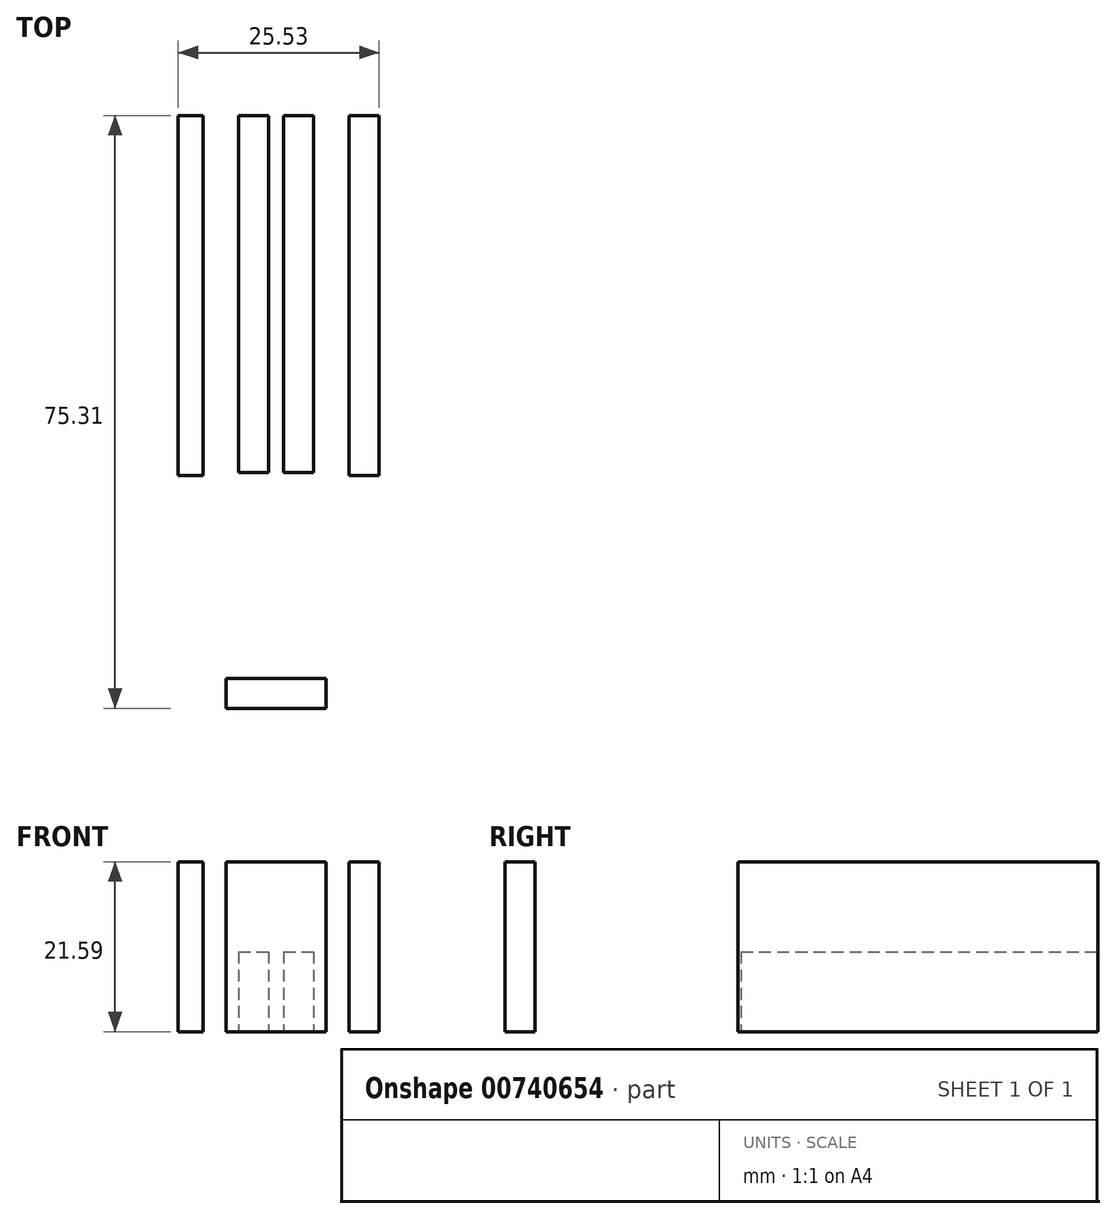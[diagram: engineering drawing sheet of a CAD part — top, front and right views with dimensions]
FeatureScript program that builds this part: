
annotation { "Feature Type Name" : "Feature", "Feature Type Description" : "" }
export const myFeature = defineFeature(function(context is Context, id is Id, definition is map)
    precondition{}
    {
        {
            var Q0;
            Q0=qCreatedBy(makeId("Top.planeOp"),FACE);
            var sketch = newSketch(context, id + "F0", { "sketchPlane" : qUnion([Q0])});
            skLineSegment(sketch, "E0", {"start": v(-8.9, 0) * mm, "end": v(8.9, 0) * mm});
            skLineSegment(sketch, "E1", {"start": v(8.9, 0) * mm, "end": v(7.62, -25.4) * mm});
            skLineSegment(sketch, "E2", {"start": v(7.62, -25.4) * mm, "end": v(-7.62, -25.4) * mm});
            skLineSegment(sketch, "E3", {"start": v(-8.9, 0) * mm, "end": v(-7.62, -25.4) * mm});
            skPoint(sketch, "E4", {"position": v(0, -25.4) * mm});
            skLineSegment(sketch, "E5", {"start": v(-15.24, -25.4) * mm, "end": v(15.24, -25.4) * mm});
            skLineSegment(sketch, "E6", {"start": v(-15.24, -25.4) * mm, "end": v(-15.24, -7.62) * mm});
            skLineSegment(sketch, "E7", {"start": v(-15.24, -7.62) * mm, "end": v(15.24, -7.62) * mm});
            skLineSegment(sketch, "E8", {"start": v(15.24, -7.62) * mm, "end": v(15.24, -25.4) * mm});
            skLineSegment(sketch, "E9", {"start": v(-15.24, -25.4) * mm, "end": v(-19.78, -36.35) * mm});
            skLineSegment(sketch, "E10", {"start": v(-19.78, -36.35) * mm, "end": v(-12.16, -36.35) * mm});
            skLineSegment(sketch, "E11", {"start": v(-12.16, -36.35) * mm, "end": v(-7.62, -25.4) * mm});
            skLineSegment(sketch, "E12.MirrorCS", {"start": v(12.16, -36.35) * mm, "end": v(7.62, -25.4) * mm});
            skLineSegment(sketch, "E13.MirrorCS", {"start": v(19.78, -36.35) * mm, "end": v(12.16, -36.35) * mm});
            skLineSegment(sketch, "E14.MirrorCS", {"start": v(15.24, -25.4) * mm, "end": v(19.78, -36.35) * mm});
            skSolve(sketch);
        }
        {
            var Q0;
            Q0=qCreatedBy(makeId("Top.planeOp"),FACE);
            var sketch = newSketch(context, id + "F1", { "sketchPlane" : qUnion([Q0])});
            skLineSegment(sketch, "E15", {"start": v(-6.35, -29.6) * mm, "end": v(6.35, -29.6) * mm});
            skLineSegment(sketch, "E16", {"start": v(6.35, -25.78) * mm, "end": v(6.35, -29.6) * mm});
            skLineSegment(sketch, "E17", {"start": v(6.35, -25.78) * mm, "end": v(-6.35, -25.78) * mm});
            skLineSegment(sketch, "E18", {"start": v(-6.35, -29.6) * mm, "end": v(-6.35, -25.78) * mm});
            skLineSegment(sketch, "E19.bottom", {"start": v(-12.45, 0) * mm, "end": v(-9.27, 0) * mm});
            skLineSegment(sketch, "E19.top", {"start": v(-12.45, 45.72) * mm, "end": v(-9.27, 45.72) * mm});
            skLineSegment(sketch, "E19.left", {"start": v(-12.45, 0) * mm, "end": v(-12.45, 45.72) * mm});
            skLineSegment(sketch, "E19.right", {"start": v(-9.27, 0) * mm, "end": v(-9.27, 45.72) * mm});
            skLineSegment(sketch, "E20.bottom", {"start": v(9.27, 0) * mm, "end": v(13.08, 0) * mm});
            skLineSegment(sketch, "E20.top", {"start": v(9.27, 45.72) * mm, "end": v(13.08, 45.72) * mm});
            skLineSegment(sketch, "E20.left", {"start": v(9.27, 0) * mm, "end": v(9.27, 45.72) * mm});
            skLineSegment(sketch, "E20.right", {"start": v(13.08, 0) * mm, "end": v(13.08, 45.72) * mm});
            skLineSegment(sketch, "E21", {"start": v(-9.27, 45.72) * mm, "end": v(9.27, 45.72) * mm});
            skPoint(sketch, "E22", {"position": v(0, 45.72) * mm});
            skPoint(sketch, "E23", {"position": v(0, -25.78) * mm});
            skLineSegment(sketch, "E24.bottom", {"start": v(-4.76, 0.38) * mm, "end": v(-0.95, 0.38) * mm});
            skLineSegment(sketch, "E24.top", {"start": v(-4.76, 45.72) * mm, "end": v(-0.95, 45.72) * mm});
            skLineSegment(sketch, "E24.left", {"start": v(-4.76, 0.38) * mm, "end": v(-4.76, 45.72) * mm});
            skLineSegment(sketch, "E24.right", {"start": v(-0.95, 0.38) * mm, "end": v(-0.95, 45.72) * mm});
            skLineSegment(sketch, "E25.bottom", {"start": v(0.95, 0.38) * mm, "end": v(4.76, 0.38) * mm});
            skLineSegment(sketch, "E25.top", {"start": v(0.95, 45.72) * mm, "end": v(4.76, 45.72) * mm});
            skLineSegment(sketch, "E25.left", {"start": v(0.95, 0.38) * mm, "end": v(0.95, 45.72) * mm});
            skLineSegment(sketch, "E25.right", {"start": v(4.76, 0.38) * mm, "end": v(4.76, 45.72) * mm});
            skLineSegment(sketch, "E26", {"start": v(-0.95, 0.38) * mm, "end": v(0.95, 0.38) * mm});
            skPoint(sketch, "E27", {"position": v(0, 0.38) * mm});
            skSolve(sketch);
        }
        {
            var Q0;
            Q0=makeQuery(id+"F1.imprint","IMPRINT",FACE,{"disambiguationData":[TD([[makeQuery(id+"F1.imprint","IMPRINT",EDGE,{"derivedFrom":sQuery(id+"F1.wireOp",EDGE,"E15")}),1.0]])]});
            var Q1;
            Q1=makeQuery(id+"F1.imprint","IMPRINT",FACE,{"disambiguationData":[TD([[makeQuery(id+"F1.imprint","IMPRINT",EDGE,{"derivedFrom":sQuery(id+"F1.wireOp",EDGE,"E19.bottom")}),1.0]])]});
            var Q2;
            Q2=makeQuery(id+"F1.imprint","IMPRINT",FACE,{"disambiguationData":[TD([[makeQuery(id+"F1.imprint","IMPRINT",EDGE,{"derivedFrom":sQuery(id+"F1.wireOp",EDGE,"E20.bottom")}),1.0]])]});
            extrude(context, id + "F2", {"entities" : qUnion([Q0, Q1, Q2]), "depth" : 21.59 * mm, "offsetDistance" : 25.4 * mm});
        }
        {
            var Q0;
            Q0=makeQuery(id+"F1.imprint","IMPRINT",FACE,{"disambiguationData":[TD([[makeQuery(id+"F1.imprint","IMPRINT",EDGE,{"derivedFrom":sQuery(id+"F1.wireOp",EDGE,"E24.bottom")}),1.0]])]});
            var Q1;
            Q1=makeQuery(id+"F1.imprint","IMPRINT",FACE,{"disambiguationData":[TD([[makeQuery(id+"F1.imprint","IMPRINT",EDGE,{"derivedFrom":sQuery(id+"F1.wireOp",EDGE,"E25.bottom")}),1.0]])]});
            extrude(context, id + "F3", {"entities" : qUnion([Q0, Q1]), "depth" : 10.16 * mm, "offsetDistance" : 25.4 * mm});
        }
    });
